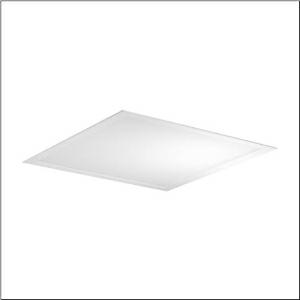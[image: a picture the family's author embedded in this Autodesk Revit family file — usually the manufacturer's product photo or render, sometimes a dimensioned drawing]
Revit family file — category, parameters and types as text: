
# Revit family: apollon_21_square_51mq11w72414
name_source: partatom
category: Lighting Fixtures
units: mm (PartAtom-declared; Revit-internal decimal feet)

## family parameters
Cut with Voids When Loaded = No
Host = Face
Light Source = No
Part Type = Normal
Room Calculation Point = No
Round Connector Dimension = Use Diameter
Shared = No

## types (1)
- Apollon 21 square (1 x LED, 4200 lm, 23.3 W, 4000K)
    Apparent Load = 23 VA
    CIE Flux Codes = 60 87 97 100 100
    Color Rendering = 80
    Color Temperature = 4000K
    Default Elevation = 1800 mm
    Description = Apollon 21 square, office luminaire, primary optical cover: micro prismatic cover, of PMMA, CAT 2 (L<= 3000cd/m²), light emission: direct distribution, primary light characteristic: symmetric, installation type: lay-in mounting, recessed, LED, rated luminous flux: 4.200lm, luminous efficacy: 180lm/W, light colour: 840, colour temperature: 4000K, control gear: ON/OFF, with terminal, 3-pole, mains connection: 220..240V, AC/DC, 0/50..60Hz, rated input power: 23.3W, suitable for self-contained emergency lighting element 59MQE002602A with integrated self-test function according to EN 60598-2-22, housing, of aluminium, coated, traffic white (RAL 9016), module: M625, length: 620mm, width: 620mm, height: 55mm, housing upper side, of sheet steel, galvanised, protection rating (complete): IP20, protection rating (lamp compartment, on room side): IP50, insulation class (complete): insulation class II (safety insulation), certification: CE, ENEC, UKCA, impact resistance: IK03, permissible operating ambient temperature: -20..+45°C, standard: EN 60598-2-22, corresponds to IFS (International Featured Standards) requirements for safety and quality in the food industry, packaging unit: 1 piece
    Height = 0 mm  [stored 0 ft]
    Lamp = 1 x LED
    Lamp Light Flux = 4200 lm
    Lamp Power = 23.3 W
    Lamp count = 1
    Length = 620 mm
    Luminous efficacy = 180 lm/W
    Manufacturer = Siteco
    ModVariant = No
    Model = 51MQ11W72414
    Mounting Place = Ceiling
    Mounting Type = Recessed
    Number of Poles = 1
    OnlyDefault = Yes
    Power Factor = 1
    Product Name = Apollon 21 square
    Product group = office luminaire | ceiling recessed
    ProductGroupID = 400
    Protection Class = Protection class II
    Protection Degree = IP 20
    RLX_Detail_Level = 1
    RLX_Emergency_Light_Flux = 0 lm
    RLX_Emergency_Type = 0
    RLX_Emergency_Type_DB = No
    RlxData = <blob elided: 13289 chars, md5=cd50ac87>
    Socket = socket
    Standby Power = 0 W
    System Light Flux = 4200 lm
    System Power = 23 W
    Type Comments = Product without accessories
    Type Image = l_1291054.jpg
    URL = http://relux.com
    VarID = ---
    Voltage = 0 V
    Weight = 0.00 kg
    Width = 620 mm

note: [stored X ft] marks values corroborated as IEEE doubles in the binary element streams (Revit-internal decimal feet)

## geometry (parser evidence)
native form markers: Sweep x11
no freeform markers — native parametric forms only
